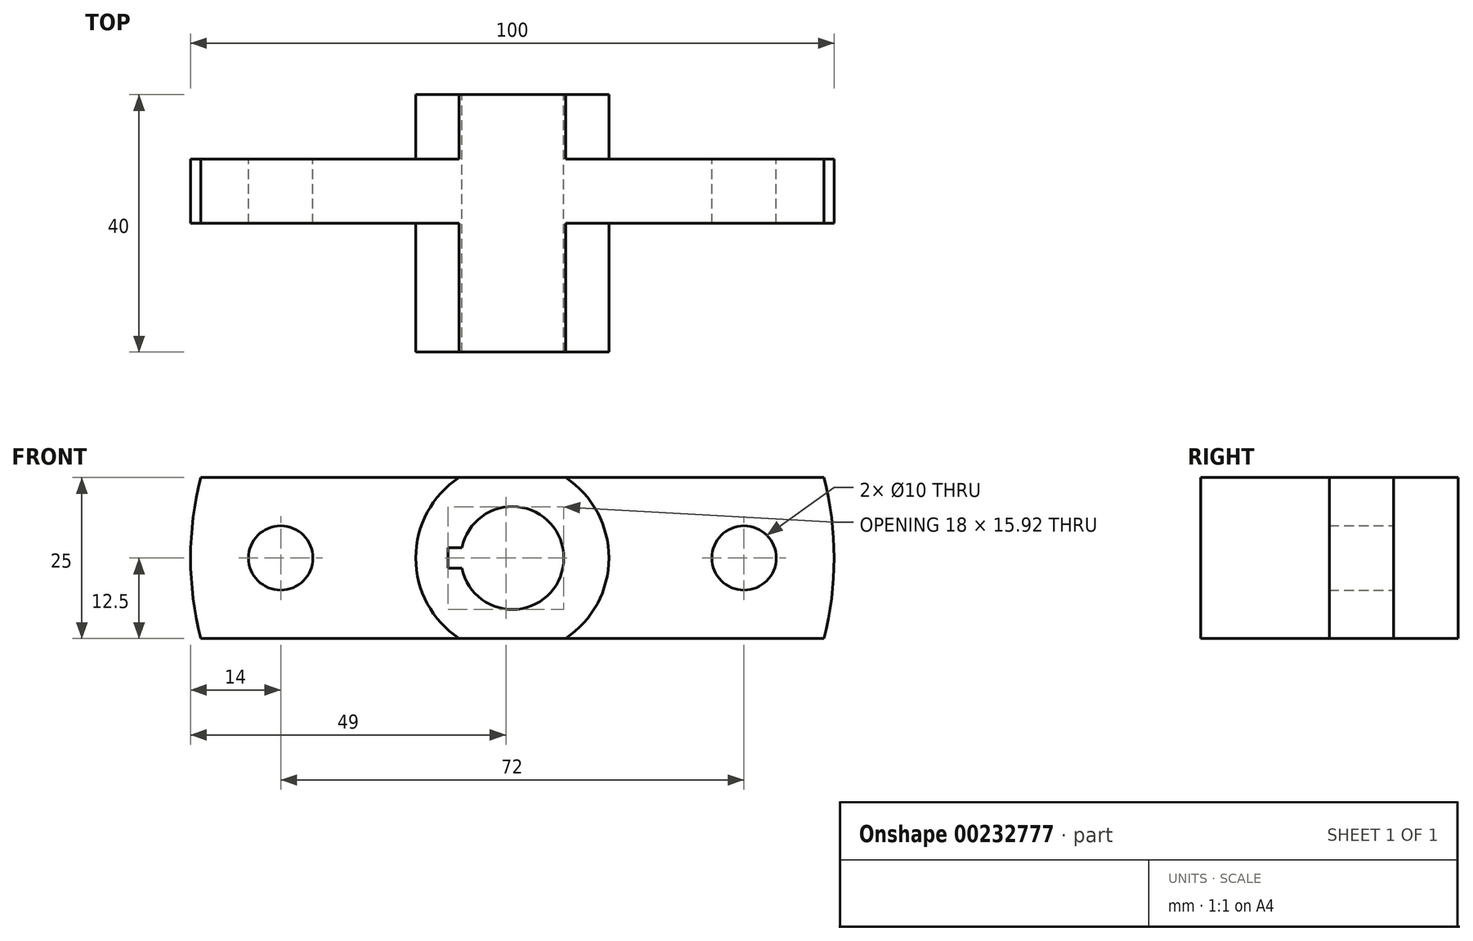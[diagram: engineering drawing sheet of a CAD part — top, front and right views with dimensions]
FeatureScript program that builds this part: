
annotation { "Feature Type Name" : "Feature", "Feature Type Description" : "" }
export const myFeature = defineFeature(function(context is Context, id is Id, definition is map)
    precondition{}
    {
        {
            var Q0;
            Q0=qCreatedBy(makeId("Front.planeOp"),FACE);
            var sketch = newSketch(context, id + "F0", { "sketchPlane" : qUnion([Q0])});
            skArc(sketch, "E0", {"start": v(-48.41, 12.5) * mm, "mid": v(-50, 0) * mm, "end": v(-48.41, -12.5) * mm});
            skArc(sketch, "E1", {"start": v(-8.3, 12.5) * mm, "mid": v(-15, 0) * mm, "end": v(-8.3, -12.5) * mm});
            skArc(sketch, "E2", {"start": v(-7.84, -1.6) * mm, "mid": v(8, 0) * mm, "end": v(-7.84, 1.6) * mm});
            skLineSegment(sketch, "E3.bottom", {"start": v(-48.41, 12.5) * mm, "end": v(48.41, 12.5) * mm});
            skLineSegment(sketch, "E3.top", {"start": v(-48.41, -12.5) * mm, "end": v(48.41, -12.5) * mm});
            skPoint(sketch, "E3.left.start.orphan", {"position": v(-65.14, 12.5) * mm});
            skPoint(sketch, "E4.orphan", {"position": v(-65.14, -12.5) * mm});
            skArc(sketch, "E5.trimOffspring", {"start": v(48.41, -12.5) * mm, "mid": v(50, 0) * mm, "end": v(48.41, 12.5) * mm});
            skPoint(sketch, "E6.orphan", {"position": v(65.14, 12.5) * mm});
            skPoint(sketch, "E7.orphan", {"position": v(65.14, -12.5) * mm});
            skArc(sketch, "E8.trimOffspring", {"start": v(8.3, -12.5) * mm, "mid": v(15, 0) * mm, "end": v(8.3, 12.5) * mm});
            skCircle(sketch, "E9", {"center": v(-36, 0) * mm, "radius": 5 * mm});
            skCircle(sketch, "E10", {"center": v(36, 0) * mm, "radius": 5 * mm});
            skLineSegment(sketch, "E11.bottom", {"start": v(-7.84, -1.6) * mm, "end": v(-10, -1.6) * mm});
            skLineSegment(sketch, "E11.top", {"start": v(-7.84, 1.6) * mm, "end": v(-10, 1.6) * mm});
            skLineSegment(sketch, "E11.right", {"start": v(-10, -1.6) * mm, "end": v(-10, 1.6) * mm});
            skPoint(sketch, "E11.middle", {"position": v(-8, 0) * mm});
            skPoint(sketch, "E11.left.end.orphan", {"position": v(-6, 1.6) * mm});
            skPoint(sketch, "E12.orphan", {"position": v(-6, -1.6) * mm});
            skSolve(sketch);
        }
        {
            var Q0;
            {var subQ1=sQuery(id+"F0.wireOp",EDGE,"E1");Q0=makeQuery(id+"F0.imprint","IMPRINT",FACE,{"disambiguationData":[TD([[makeQuery(id+"F0.imprint","IMPRINT",EDGE,{"derivedFrom":subQ1}),1.0]])]});}
            extrude(context, id + "F1", {"entities" : qUnion([Q0]), "depth" : 30 * mm, "hasSecondDirection" : true, "secondDirectionOppositeDirection" : true, "secondDirectionDepth" : 10 * mm});
        }
        {
            var Q0;
            Q0 = qSketchRegion(id + "F0", true);
            extrude(context, id + "F2", {"entities" : qUnion([Q0]), "operationType" : NewBodyOperationType.ADD, "depth" : 10 * mm});
        }
    });
